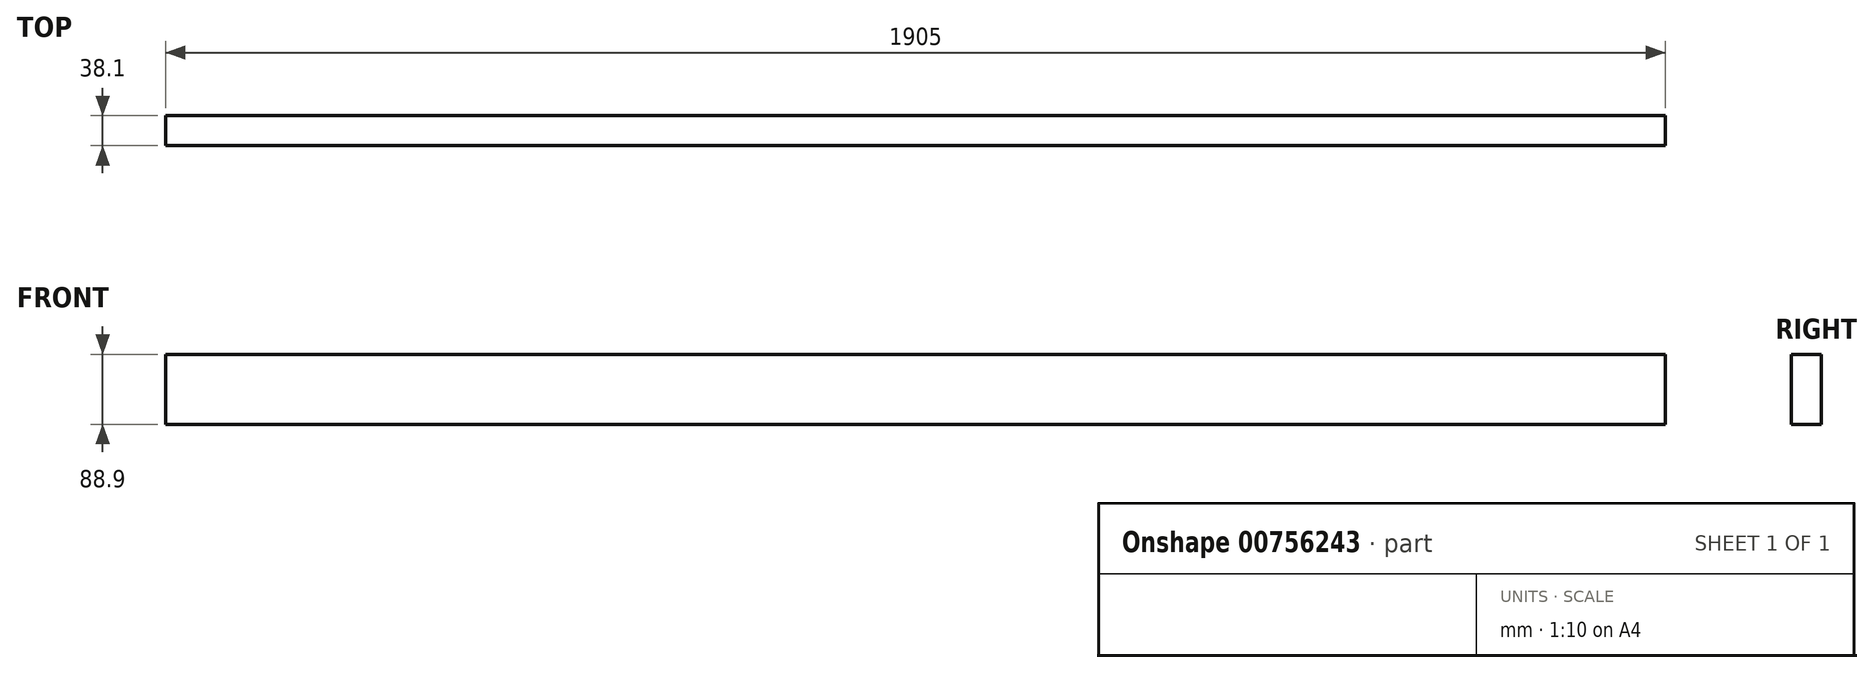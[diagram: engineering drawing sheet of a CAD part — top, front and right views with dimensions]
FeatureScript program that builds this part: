
annotation { "Feature Type Name" : "Feature", "Feature Type Description" : "" }
export const myFeature = defineFeature(function(context is Context, id is Id, definition is map)
    precondition{}
    {
        {
            var Q0;
            Q0=qCreatedBy(makeId("Front.planeOp"),FACE);
            var sketch = newSketch(context, id + "F0", { "sketchPlane" : qUnion([Q0])});
            skLineSegment(sketch, "E0.bottom", {"start": v(0, 0) * mm, "end": v(1905, 0) * mm});
            skLineSegment(sketch, "E0.top", {"start": v(0, -88.9) * mm, "end": v(1905, -88.9) * mm});
            skLineSegment(sketch, "E0.left", {"start": v(0, 0) * mm, "end": v(0, -88.9) * mm});
            skLineSegment(sketch, "E0.right", {"start": v(1905, 0) * mm, "end": v(1905, -88.9) * mm});
            skSolve(sketch);
        }
        {
            var Q0;
            Q0=makeQuery(id+"F0.imprint","IMPRINT",FACE,{"disambiguationData":[TD([[makeQuery(id+"F0.imprint","IMPRINT",EDGE,{"derivedFrom":sQuery(id+"F0.wireOp",EDGE,"E0.bottom")}),-1.0]])]});
            extrude(context, id + "F1", {"entities" : qUnion([Q0]), "depth" : 38.1 * mm, "offsetDistance" : 25.4 * mm});
        }
    });
